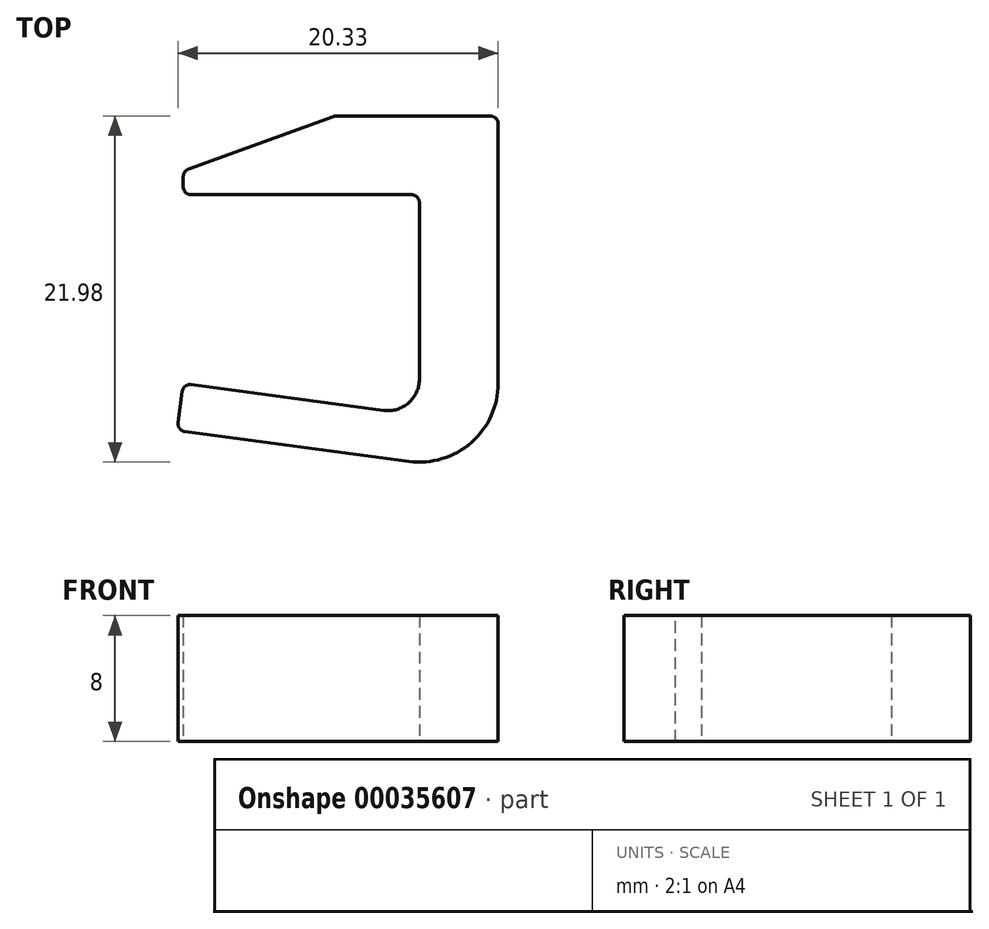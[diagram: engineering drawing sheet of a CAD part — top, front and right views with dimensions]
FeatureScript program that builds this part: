
annotation { "Feature Type Name" : "Feature", "Feature Type Description" : "" }
export const myFeature = defineFeature(function(context is Context, id is Id, definition is map)
    precondition{}
    {
        {
            var Q0;
            Q0=qCreatedBy(makeId("Top.planeOp"),FACE);
            var sketch = newSketch(context, id + "F0", { "sketchPlane" : qUnion([Q0])});
            skLineSegment(sketch, "E0", {"start": v(0, 0) * mm, "end": v(0, 14) * mm});
            skLineSegment(sketch, "E1", {"start": v(0, 14) * mm, "end": v(-15, 14) * mm});
            skLineSegment(sketch, "E2", {"start": v(-15, 14) * mm, "end": v(-15, 15.5) * mm});
            skLineSegment(sketch, "E3", {"start": v(-15, 15.5) * mm, "end": v(-5.38, 19) * mm});
            skLineSegment(sketch, "E4", {"start": v(-5.38, 19) * mm, "end": v(5, 19) * mm});
            skLineSegment(sketch, "E5", {"start": v(5, 19) * mm, "end": v(5, -3.7) * mm});
            skLineSegment(sketch, "E6", {"start": v(5, -3.7) * mm, "end": v(-15.4, -0.97) * mm});
            skLineSegment(sketch, "E7", {"start": v(-15.4, -0.97) * mm, "end": v(-15, 2) * mm});
            skLineSegment(sketch, "E8", {"start": v(-15, 2) * mm, "end": v(0, 0) * mm});
            skSolve(sketch);
        }
        {
            var Q0;
            Q0=makeQuery(id+"F0.imprint","IMPRINT",FACE,{"disambiguationData":[TD([[makeQuery(id+"F0.imprint","IMPRINT",EDGE,{"derivedFrom":sQuery(id+"F0.wireOp",EDGE,"E0")}),-1.0]])]});
            extrude(context, id + "F1", {"entities" : qUnion([Q0]), "depth" : 8 * mm});
        }
        {
            var Q0;
            Q0=makeQuery(id+"F1.opExtrude","SWEPT_EDGE",EDGE,{"disambiguationData":[OSD([sQuery(id+"F0.wireOp",EDGE,"E0"),sQuery(id+"F0.wireOp",EDGE,"E8")])]});
            fillet(context, id + "F2", {"entities" : qUnion([Q0]), "radius" : 2 * mm, "tangentPropagation" : true, "allowEdgeOverflow" : false});
        }
        {
            var Q0;
            Q0=makeQuery(id+"F1.opExtrude","SWEPT_EDGE",EDGE,{"disambiguationData":[OSD([sQuery(id+"F0.wireOp",EDGE,"E1"),sQuery(id+"F0.wireOp",EDGE,"E2")])]});
            var Q1;
            Q1=makeQuery(id+"F1.opExtrude","SWEPT_EDGE",EDGE,{"disambiguationData":[OSD([sQuery(id+"F0.wireOp",EDGE,"E7"),sQuery(id+"F0.wireOp",EDGE,"E8")])]});
            var Q2;
            Q2=makeQuery(id+"F1.opExtrude","SWEPT_EDGE",EDGE,{"disambiguationData":[OSD([sQuery(id+"F0.wireOp",EDGE,"E6"),sQuery(id+"F0.wireOp",EDGE,"E7")])]});
            var Q3;
            Q3=makeQuery(id+"F1.opExtrude","SWEPT_EDGE",EDGE,{"disambiguationData":[OSD([sQuery(id+"F0.wireOp",EDGE,"E2"),sQuery(id+"F0.wireOp",EDGE,"E3")])]});
            var Q4;
            Q4=makeQuery(id+"F1.opExtrude","SWEPT_EDGE",EDGE,{"disambiguationData":[OSD([sQuery(id+"F0.wireOp",EDGE,"E3"),sQuery(id+"F0.wireOp",EDGE,"E4")])]});
            var Q5;
            Q5=makeQuery(id+"F1.opExtrude","SWEPT_EDGE",EDGE,{"disambiguationData":[OSD([sQuery(id+"F0.wireOp",EDGE,"E0"),sQuery(id+"F0.wireOp",EDGE,"E1")])]});
            var Q6;
            Q6=makeQuery(id+"F1.opExtrude","SWEPT_EDGE",EDGE,{"disambiguationData":[OSD([sQuery(id+"F0.wireOp",EDGE,"E4"),sQuery(id+"F0.wireOp",EDGE,"E5")])]});
            fillet(context, id + "F3", {"entities" : qUnion([Q0, Q1, Q2, Q3, Q4, Q5, Q6]), "radius" : .5 * mm, "tangentPropagation" : true, "allowEdgeOverflow" : false});
        }
        {
            var Q0;
            Q0=makeQuery(id+"F1.opExtrude","SWEPT_EDGE",EDGE,{"disambiguationData":[OSD([sQuery(id+"F0.wireOp",EDGE,"E5"),sQuery(id+"F0.wireOp",EDGE,"E6")])]});
            fillet(context, id + "F4", {"entities" : qUnion([Q0]), "radius" : 5 * mm, "tangentPropagation" : true, "allowEdgeOverflow" : false});
        }
    });
